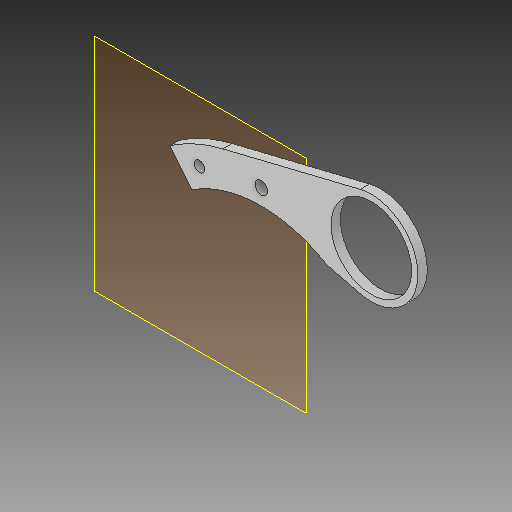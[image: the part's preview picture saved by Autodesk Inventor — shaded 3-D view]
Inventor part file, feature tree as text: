
AUTODESK INVENTOR PART (.ipt)
format: ipt  version: 2019.3 (Build 233278000, 278)  size: 105,472 bytes
history: native  units: mm
features: other x3, reference x2, plane x1, extrude x1, sketch x1
ambient origin geometry x8: Origin, YZ Plane, XZ Plane, XY Plane, X Axis, Y Axis, Z Axis, Center Point
bodies: Solid1 (feature_tree)
feature tree (8):
  plane  "Work Plane1"
  extrude  "Extrusion1"  [1 undecoded]
  sketch  "Sketch1"  dims[d0=4.4mm d1=0.0mm]
  reference  "Reference2"
  reference  "Reference3"
  other  "<userpath>\Desktop\3dprojects\OpenEmoto\Swingarm3\Swingarm3.iam"
  other  "Swingarm3.iam"
  other  "FrontMotorPlateBridge:1"
note: 1 required parameter value undecoded (feature->parameter linkage not recoverable at this tier; creation-order binding heuristic only, values carry confidence <= 0.55)
